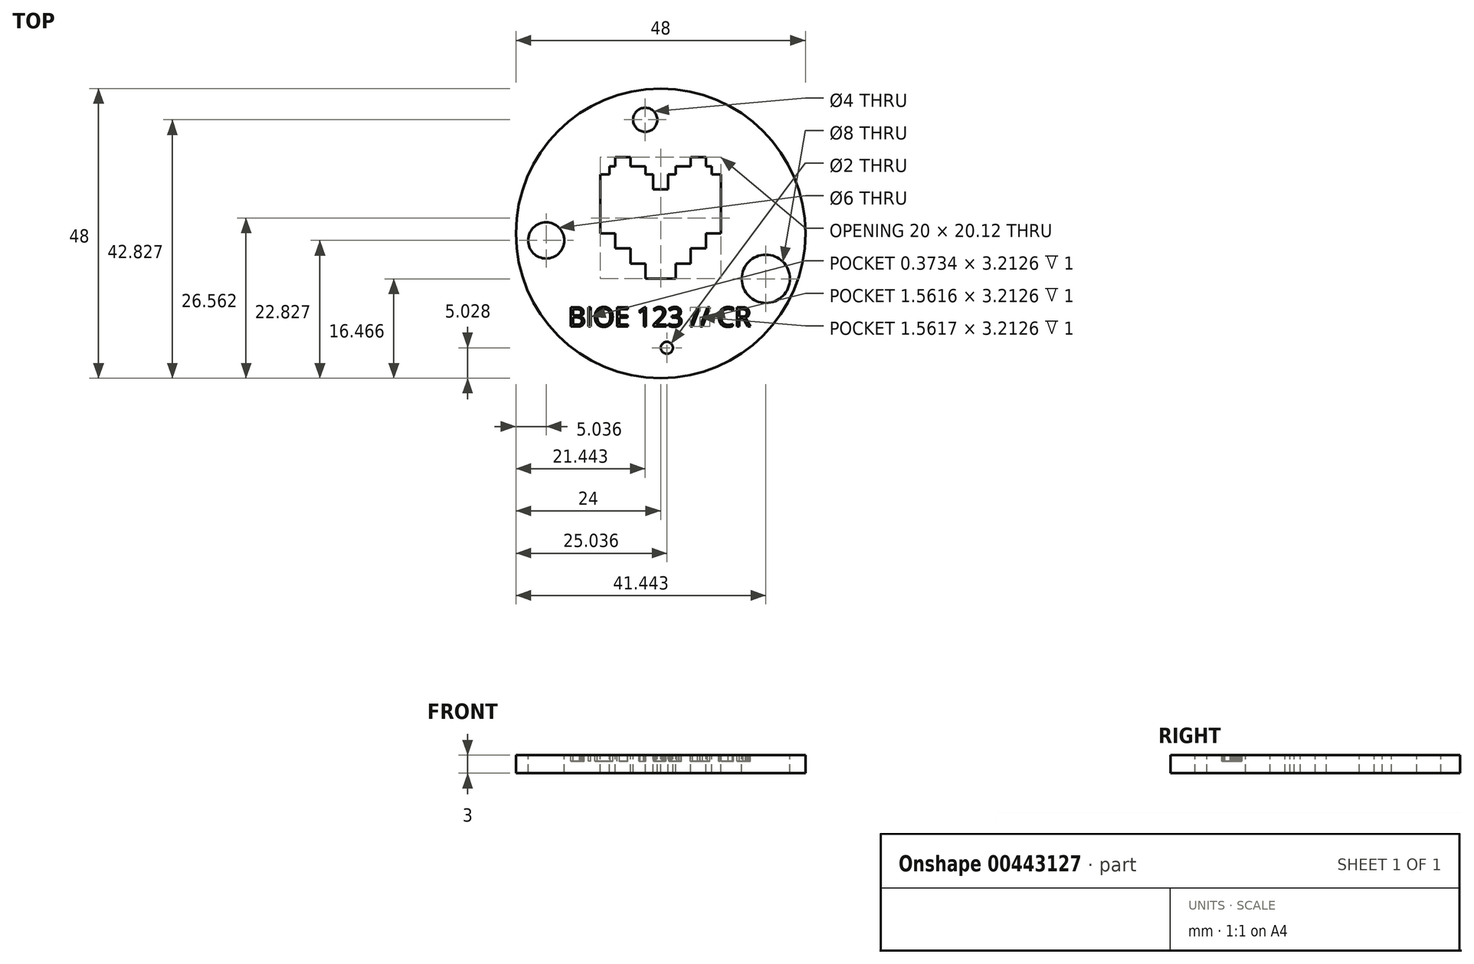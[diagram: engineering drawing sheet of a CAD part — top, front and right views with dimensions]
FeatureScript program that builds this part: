
annotation { "Feature Type Name" : "Feature", "Feature Type Description" : "" }
export const myFeature = defineFeature(function(context is Context, id is Id, definition is map)
    precondition{}
    {
        {
            var Q0;
            Q0=qCreatedBy(makeId("Top.planeOp"),FACE);
            var sketch = newSketch(context, id + "F0", { "sketchPlane" : qUnion([Q0])});
            skCircle(sketch, "E0", {"center": v(0, 0) * mm, "radius": 24 * mm});
            skSolve(sketch);
        }
        {
            var Q0;
            Q0=sQuery(id+"F0.wireOp",EDGE,"E0");
            extrude(context, id + "F1", {"bodyType" : ToolBodyType.SURFACE, "surfaceEntities" : qUnion([Q0]), "oppositeDirection" : true, "depth" : 3 * mm});
        }
        {
            var Q0;
            Q0=qCreatedBy(makeId("Top.planeOp"),FACE);
            var sketch = newSketch(context, id + "F2", { "sketchPlane" : qUnion([Q0])});
            skCircle(sketch, "E1", {"center": v(0, 0) * mm, "radius": 24 * mm});
            skSolve(sketch);
        }
        {
            var Q0;
            Q0=makeQuery(id+"F2.imprint","IMPRINT",FACE,{"disambiguationData":[TD([[makeQuery(id+"F2.imprint","IMPRINT",EDGE,{"derivedFrom":sQuery(id+"F2.wireOp",EDGE,"E1")}),1.0]])]});
            extrude(context, id + "F3", {"entities" : qUnion([Q0]), "oppositeDirection" : true, "depth" : 3 * mm});
        }
        {
            var Q0;
            Q0=qCreatedBy(makeId("Top.planeOp"),FACE);
            var sketch = newSketch(context, id + "F4", { "sketchPlane" : qUnion([Q0])});
            skCircle(sketch, "E2", {"center": v(-2.56, 18.83) * mm, "radius": 2 * mm});
            skCircle(sketch, "E3", {"center": v(17.44, -7.53) * mm, "radius": 4 * mm});
            skCircle(sketch, "E4", {"center": v(-18.96, -1.17) * mm, "radius": 3 * mm});
            skCircle(sketch, "E5", {"center": v(1.04, -18.97) * mm, "radius": 1 * mm});
            skSolve(sketch);
        }
        {
            var Q0;
            Q0=makeQuery(id+"F4.imprint","IMPRINT",FACE,{"disambiguationData":[TD([[makeQuery(id+"F4.imprint","IMPRINT",EDGE,{"derivedFrom":sQuery(id+"F4.wireOp",EDGE,"E4")}),1.0]])]});
            var Q1;
            Q1=makeQuery(id+"F4.imprint","IMPRINT",FACE,{"disambiguationData":[TD([[makeQuery(id+"F4.imprint","IMPRINT",EDGE,{"derivedFrom":sQuery(id+"F4.wireOp",EDGE,"E5")}),1.0]])]});
            var Q2;
            Q2=makeQuery(id+"F4.imprint","IMPRINT",FACE,{"disambiguationData":[TD([[makeQuery(id+"F4.imprint","IMPRINT",EDGE,{"derivedFrom":sQuery(id+"F4.wireOp",EDGE,"E3")}),1.0]])]});
            var Q3;
            Q3=makeQuery(id+"F4.imprint","IMPRINT",FACE,{"disambiguationData":[TD([[makeQuery(id+"F4.imprint","IMPRINT",EDGE,{"derivedFrom":sQuery(id+"F4.wireOp",EDGE,"E2")}),1.0]])]});
            extrude(context, id + "F5", {"entities" : qUnion([Q0, Q1, Q2, Q3]), "operationType" : NewBodyOperationType.REMOVE, "endBound" : BoundingType.THROUGH_ALL, "oppositeDirection" : true, "depth" : 25 * mm});
        }
        {
            var Q0;
            Q0=qCreatedBy(makeId("Top.planeOp"),FACE);
            var sketch = newSketch(context, id + "F6", { "sketchPlane" : qUnion([Q0])});
            skLineSegment(sketch, "E6", {"start": v(0, -7.5) * mm, "end": v(2.5, -7.5) * mm});
            skLineSegment(sketch, "E7", {"start": v(2.5, -7.5) * mm, "end": v(2.5, -5) * mm});
            skLineSegment(sketch, "E8", {"start": v(2.5, -5) * mm, "end": v(5, -5) * mm});
            skLineSegment(sketch, "E9", {"start": v(5, -5) * mm, "end": v(5, -2.5) * mm});
            skLineSegment(sketch, "E10", {"start": v(5, -2.5) * mm, "end": v(7.5, -2.5) * mm});
            skLineSegment(sketch, "E11", {"start": v(7.5, -2.5) * mm, "end": v(7.5, 0) * mm});
            skLineSegment(sketch, "E12", {"start": v(7.5, 0) * mm, "end": v(10, 0) * mm});
            skLineSegment(sketch, "E13", {"start": v(10, 0) * mm, "end": v(10, 9.8) * mm});
            skLineSegment(sketch, "E14", {"start": v(10, 9.8) * mm, "end": v(8.5, 9.8) * mm});
            skLineSegment(sketch, "E15", {"start": v(8.5, 9.8) * mm, "end": v(8.5, 11.12) * mm});
            skLineSegment(sketch, "E16", {"start": v(8.5, 11.12) * mm, "end": v(7.5, 11.12) * mm});
            skLineSegment(sketch, "E17", {"start": v(7.5, 11.12) * mm, "end": v(7.5, 12.62) * mm});
            skLineSegment(sketch, "E18", {"start": v(7.5, 12.62) * mm, "end": v(5, 12.62) * mm});
            skLineSegment(sketch, "E19", {"start": v(5, 12.62) * mm, "end": v(5, 11.12) * mm});
            skLineSegment(sketch, "E20", {"start": v(5, 11.12) * mm, "end": v(2.5, 11.12) * mm});
            skLineSegment(sketch, "E21", {"start": v(2.5, 11.12) * mm, "end": v(2.5, 9.8) * mm});
            skLineSegment(sketch, "E22", {"start": v(2.5, 9.8) * mm, "end": v(1.25, 9.8) * mm});
            skLineSegment(sketch, "E23", {"start": v(1.25, 9.8) * mm, "end": v(1.25, 7.3) * mm});
            skLineSegment(sketch, "E24", {"start": v(1.25, 7.3) * mm, "end": v(0, 7.3) * mm});
            skLineSegment(sketch, "E25.MirrorCS", {"start": v(-1.25, 7.3) * mm, "end": v(0, 7.3) * mm});
            skLineSegment(sketch, "E26.MirrorCS", {"start": v(-7.5, 12.62) * mm, "end": v(-5, 12.62) * mm});
            skLineSegment(sketch, "E27.MirrorCS", {"start": v(-7.5, 11.12) * mm, "end": v(-7.5, 12.62) * mm});
            skLineSegment(sketch, "E28.MirrorCS", {"start": v(-8.5, 11.12) * mm, "end": v(-7.5, 11.12) * mm});
            skLineSegment(sketch, "E29.MirrorCS", {"start": v(-5, 12.62) * mm, "end": v(-5, 11.12) * mm});
            skLineSegment(sketch, "E30.MirrorCS", {"start": v(-5, 11.12) * mm, "end": v(-2.5, 11.12) * mm});
            skLineSegment(sketch, "E31.MirrorCS", {"start": v(-7.5, 0) * mm, "end": v(-10, 0) * mm});
            skLineSegment(sketch, "E32.MirrorCS", {"start": v(-10, 0) * mm, "end": v(-10, 9.8) * mm});
            skLineSegment(sketch, "E33.MirrorCS", {"start": v(-7.5, -2.5) * mm, "end": v(-7.5, 0) * mm});
            skLineSegment(sketch, "E34.MirrorCS", {"start": v(-5, -5) * mm, "end": v(-5, -2.5) * mm});
            skLineSegment(sketch, "E35.MirrorCS", {"start": v(-2.5, 11.12) * mm, "end": v(-2.5, 9.8) * mm});
            skLineSegment(sketch, "E36.MirrorCS", {"start": v(-5, -2.5) * mm, "end": v(-7.5, -2.5) * mm});
            skLineSegment(sketch, "E37.MirrorCS", {"start": v(0, -7.5) * mm, "end": v(-2.5, -7.5) * mm});
            skLineSegment(sketch, "E38.MirrorCS", {"start": v(-2.5, 9.8) * mm, "end": v(-1.25, 9.8) * mm});
            skLineSegment(sketch, "E39.MirrorCS", {"start": v(-1.25, 9.8) * mm, "end": v(-1.25, 7.3) * mm});
            skLineSegment(sketch, "E40.MirrorCS", {"start": v(-10, 9.8) * mm, "end": v(-8.5, 9.8) * mm});
            skLineSegment(sketch, "E41.MirrorCS", {"start": v(-8.5, 9.8) * mm, "end": v(-8.5, 11.12) * mm});
            skLineSegment(sketch, "E42.MirrorCS", {"start": v(-2.5, -7.5) * mm, "end": v(-2.5, -5) * mm});
            skLineSegment(sketch, "E43.MirrorCS", {"start": v(-2.5, -5) * mm, "end": v(-5, -5) * mm});
            skSolve(sketch);
        }
        {
            var Q0;
            Q0 = qSketchRegion(id + "F6", true);
            extrude(context, id + "F7", {"entities" : qUnion([Q0]), "operationType" : NewBodyOperationType.REMOVE, "endBound" : BoundingType.THROUGH_ALL, "oppositeDirection" : true, "depth" : 25 * mm});
        }
        {
            var Q0;
            Q0=qCreatedBy(makeId("Top.planeOp"),FACE);
            var sketch = newSketch(context, id + "F8", { "sketchPlane" : qUnion([Q0])});
            skText(sketch, "E44", { "text": "BIOE 123 // CR", "fontName": "OpenSans-Regular.ttf"});
            const initialGuessF8  = {"E44": [-0.01534, -0.01546, 1, 0, 0.00324]};
            skSetInitialGuess(sketch, initialGuessF8);
            skSolve(sketch);
        }
        {
            var Q0;
            Q0 = qSketchRegion(id + "F8", true);
            extrude(context, id + "F9", {"entities" : qUnion([Q0]), "operationType" : NewBodyOperationType.REMOVE, "oppositeDirection" : true, "depth" : 1 * mm});
        }
    });
